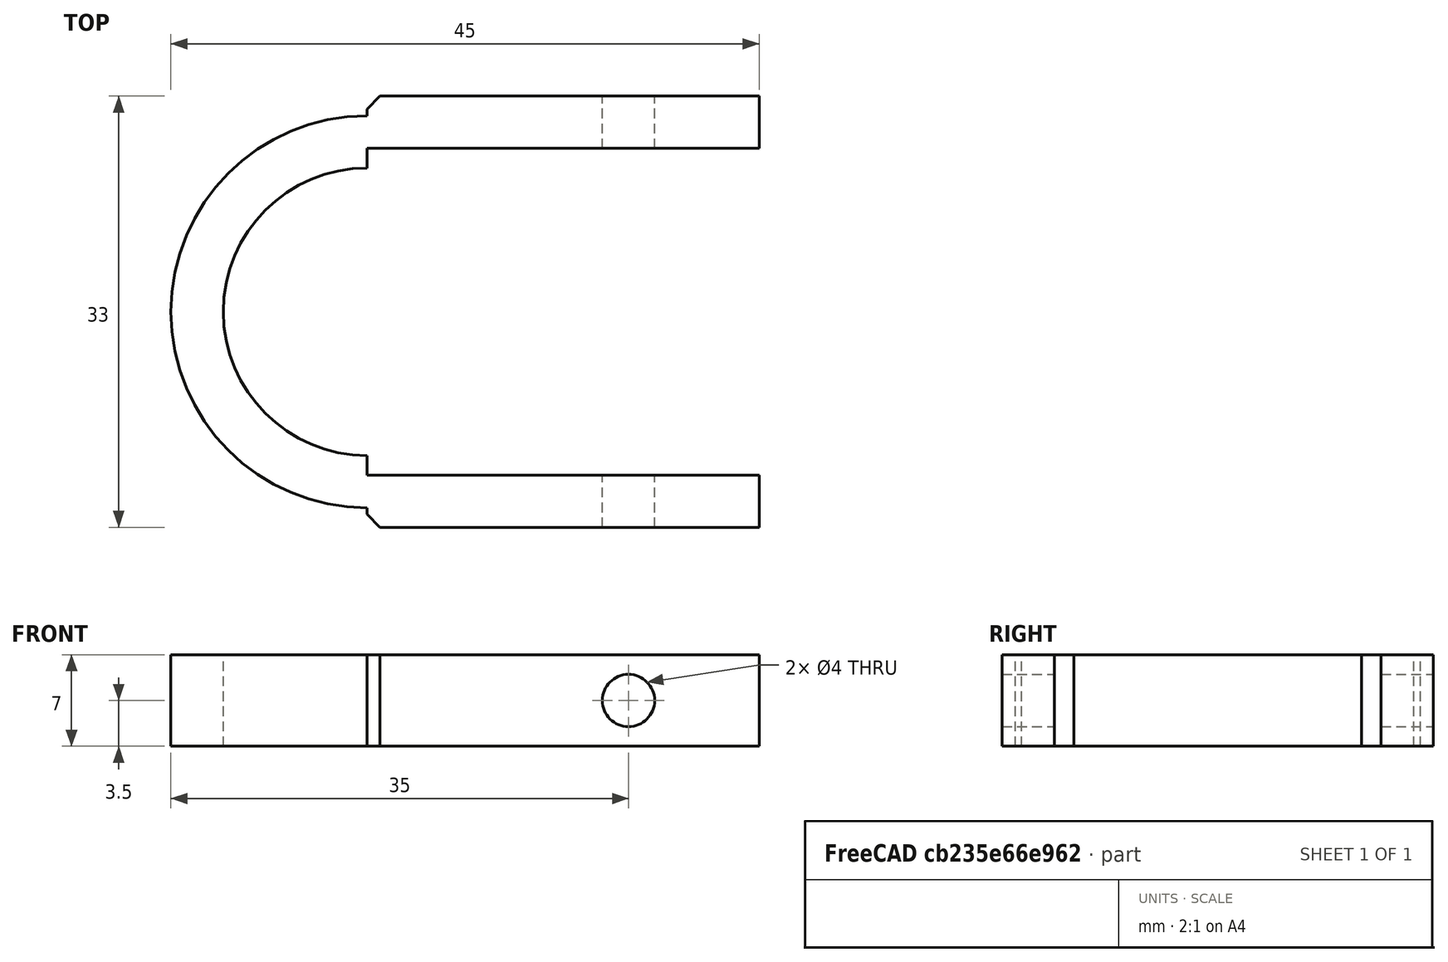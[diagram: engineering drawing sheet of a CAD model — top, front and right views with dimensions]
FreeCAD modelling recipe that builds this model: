
FCSTD DOCUMENT  (FreeCAD 0.17R13522 (Git))
Label: connector-bearing-cap
License: All rights reserved
LicenseURL: http://en.wikipedia.org/wiki/All_rights_reserved
objects: Part::Cylinder×3, Part::Box×2, Part::MultiFuse×2, Part::Cut×1, Part::Chamfer×1
note: 9 computed .brp shape members not serialized (recipe doc carries the construction recipe); baked Part::Feature solids carry a one-line shape summary decoded from their .brp

FEATURE [Part::Cylinder] Cylinder  label="Bearing"
  Angle = 360
  AttacherType = Attacher::AttachEngine3D
  Height = 7
  Placement = pos=(0,0,-3.5) rot=(0,0,1;0rad)
  Radius = 11
FEATURE [Part::Cylinder] Cylinder001  label="BearingOuter"
  Angle = 360
  AttacherType = Attacher::AttachEngine3D
  Height = 7
  Placement = pos=(0,0,-3.5) rot=(0,0,1;0rad)
  Radius = 15
FEATURE [Part::Box] Box  label="Cube"
  AttacherType = Attacher::AttachEngine3D
  Height = 7
  Length = 30
  Placement = pos=(0,-16.5,-3.5) rot=(0,0,1;0rad)
  Width = 33
FEATURE [Part::Box] Box001  label="Cube001"
  AttacherType = Attacher::AttachEngine3D
  Height = 7
  Length = 30
  Placement = pos=(0,-12.5,-3.5) rot=(0,0,1;0rad)
  Width = 25
FEATURE [Part::MultiFuse] Fusion  label="Positive Fusion"
  Shapes = -> [Box,Cylinder001]
FEATURE [Part::Cylinder] Cylinder002  label="Screw"
  Angle = 360
  AttacherType = Attacher::AttachEngine3D
  Height = 40
  Placement = pos=(20,-20,0) rot=(1,0,0;4.71239rad)
  Radius = 2
FEATURE [Part::MultiFuse] Fusion001  label="Negative Fusion"
  Shapes = -> [Cylinder,Box001,Cylinder002]
FEATURE [Part::Cut] Cut
  Base = -> Fusion
  Tool = -> Fusion001
FEATURE [Part::Chamfer] Chamfer
  Base = -> Cut
  Edges = 2 edges r=1: [Edge3,Edge36]
